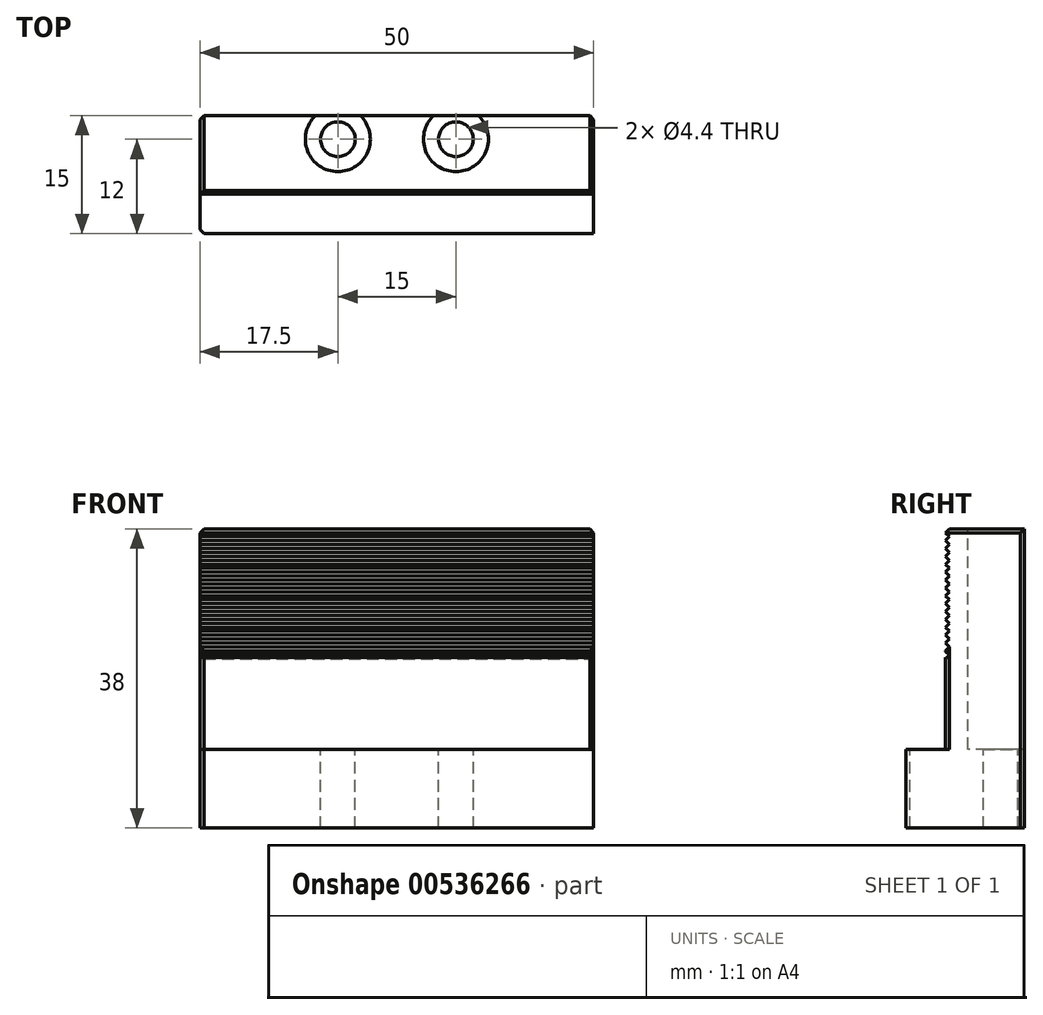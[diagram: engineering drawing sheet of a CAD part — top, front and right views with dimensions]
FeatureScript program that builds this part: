
annotation { "Feature Type Name" : "Feature", "Feature Type Description" : "" }
export const myFeature = defineFeature(function(context is Context, id is Id, definition is map)
    precondition{}
    {
        {
            var Q0;
            Q0=qCreatedBy(makeId("Front.planeOp"),FACE);
            var sketch = newSketch(context, id + "F0", { "sketchPlane" : qUnion([Q0])});
            skLineSegment(sketch, "E0.bottom", {"start": v(0, 0) * mm, "end": v(50, 0) * mm});
            skLineSegment(sketch, "E0.top", {"start": v(0, -38) * mm, "end": v(50, -38) * mm});
            skLineSegment(sketch, "E0.left", {"start": v(0, 0) * mm, "end": v(0, -38) * mm});
            skLineSegment(sketch, "E0.right", {"start": v(50, 0) * mm, "end": v(50, -38) * mm});
            skSolve(sketch);
        }
        {
            var Q0;
            Q0 = qSketchRegion(id + "FYO4Oi6wWd3sull_0", true);
            var Q1;
            Q1=makeQuery(id+"F0.imprint","IMPRINT",FACE,{"disambiguationData":[TD([[makeQuery(id+"F0.imprint","IMPRINT",EDGE,{"derivedFrom":sQuery(id+"F0.wireOp",EDGE,"E0.bottom")}),-1.0]])]});
            extrude(context, id + "F1", {"entities" : qUnion([Q0, Q1]), "depth" : 10 * mm, "offsetDistance" : 25 * mm});
        }
        {
            var Q0;
            Q0=makeQuery(id+"F1.opExtrude","CAP_FACE",FACE,{"disambiguationData":[OSD([sQuery(id+"F0.wireOp",EDGE,"E0.bottom"),sQuery(id+"F0.wireOp",EDGE,"E0.top"),sQuery(id+"F0.wireOp",EDGE,"E0.left"),sQuery(id+"F0.wireOp",EDGE,"E0.right")])],"isStart":false});
            var sketch = newSketch(context, id + "F2", { "sketchPlane" : qUnion([Q0])});
            skLineSegment(sketch, "E1.bottom", {"start": v(0, -38) * mm, "end": v(50, -38) * mm});
            skLineSegment(sketch, "E1.top", {"start": v(0, -28) * mm, "end": v(50, -28) * mm});
            skLineSegment(sketch, "E1.left", {"start": v(0, -38) * mm, "end": v(0, -28) * mm});
            skLineSegment(sketch, "E1.right", {"start": v(50, -38) * mm, "end": v(50, -28) * mm});
            skSolve(sketch);
        }
        {
            var Q0;
            Q0=makeQuery(id+"F2.imprint","IMPRINT",FACE,{"disambiguationData":[TD([[makeQuery(id+"F2.imprint","IMPRINT",EDGE,{"derivedFrom":sQuery(id+"F2.wireOp",EDGE,"E1.bottom")}),1.0]])]});
            extrude(context, id + "F3", {"entities" : qUnion([Q0]), "operationType" : NewBodyOperationType.ADD, "depth" : 5 * mm, "offsetDistance" : 25 * mm});
        }
        {
            var Q0;
            Q0=qCreatedBy(makeId("Top.planeOp"),FACE);
            var sketch = newSketch(context, id + "F4", { "sketchPlane" : qUnion([Q0])});
            skPoint(sketch, "E2", {"position": v(17.5, -3) * mm});
            skPoint(sketch, "E3", {"position": v(32.5, -3) * mm});
            skSolve(sketch);
        }
        {
            var Q0;
            Q0=sQuery(id+"F4.wireOp",VERTEX,"E2");
            var Q1;
            Q1=sQuery(id+"F4.wireOp",VERTEX,"E3");
            var Q2;
            Q2=makeQuery(id+"F1.opExtrude","SWEPT_BODY",BODY,{"disambiguationData":[OSD([sQuery(id+"F0.wireOp",EDGE,"E0.bottom"),sQuery(id+"F0.wireOp",EDGE,"E0.top"),sQuery(id+"F0.wireOp",EDGE,"E0.left"),sQuery(id+"F0.wireOp",EDGE,"E0.right")])]});
            hole(context, id + "F5", {"style" : HoleStyle.C_BORE, "endStyle" : HoleEndStyle.THROUGH, "holeDiameter" : 4.4 * mm, "cBoreDiameter" : 8.25 * mm, "cBoreDepth" : 28 * mm, "isTappedThrough" : true, "tappedDepth" : 50 * mm, "tapClearance" : 3, "startFromSketch" : true, "locations" : qUnion([Q0, Q1]), "scope" : qUnion([Q2])});
        }
        {
            var Q0;
            Q0=makeQuery(id+"F3.boolean.opBoolean","MERGE",FACE,{"derivedFrom":[makeQuery(id+"F1.opExtrude","SWEPT_FACE",FACE,{"disambiguationData":[OSD([sQuery(id+"F0.wireOp",EDGE,"E0.right")])]}),makeQuery(id+"F3.opExtrude","SWEPT_FACE",FACE,{"disambiguationData":[OSD([sQuery(id+"F2.wireOp",EDGE,"E1.right")])]})]});
            var sketch = newSketch(context, id + "F6", { "sketchPlane" : qUnion([Q0])});
            skSolve(sketch);
        }
        {
            var Q0;
            Q0=makeQuery(id+"F1.opExtrude","CAP_EDGE",EDGE,{"disambiguationData":[OSD([sQuery(id+"F0.wireOp",EDGE,"E0.bottom")])],"isStart":false});
            chamfer(context, id + "F7", {"entities" : qUnion([Q0]), "width" : .5 * mm, "tangentPropagation" : true});
        }
        {
            var Q0;
            {var subQ1=sQuery(id+"F0.wireOp",EDGE,"E0.right");Q0=makeQuery(id+"F6.imprint","IMPRINT",FACE,{"disambiguationData":[TD([[makeQuery(id+"F6.imprint","IMPRINT",EDGE,{"derivedFrom":makeQuery(id+"F1.opExtrude","CAP_EDGE",EDGE,{"disambiguationData":[OSD([subQ1])],"isStart":true})}),-1.0]])]});}
            var sketch = newSketch(context, id + "F8", { "sketchPlane" : qUnion([Q0])});
            skPoint(sketch, "E4", {"position": v(-10.03, -0.5) * mm});
            skPoint(sketch, "E5", {"position": v(-10, -1.5) * mm});
            skPoint(sketch, "E6", {"position": v(-9.5, -1) * mm});
            skLineSegment(sketch, "E7", {"start": v(-10.03, -0.5) * mm, "end": v(-9.5, -1) * mm});
            skLineSegment(sketch, "E8", {"start": v(-10, -1.5) * mm, "end": v(-10.03, -0.5) * mm});
            skLineSegment(sketch, "E9", {"start": v(-9.5, -1) * mm, "end": v(-10, -1.5) * mm});
            skSolve(sketch);
        }
        {
            var Q0;
            Q0 = qSketchRegion(id + "FoSwPSxo0hVtyaT_1", true);
            var Q1;
            {var subQ0=sQuery(id+"F8.wireOp",EDGE,"E9");Q1=makeQuery(id+"F8.imprint","IMPRINT",FACE,{"disambiguationData":[TD([[makeQuery(id+"F8.imprint","IMPRINT",EDGE,{"derivedFrom":subQ0}),-1.0]])]});}
            extrude(context, id + "F9", {"entities" : qUnion([Q0, Q1]), "operationType" : NewBodyOperationType.REMOVE, "endBound" : BoundingType.THROUGH_ALL, "oppositeDirection" : true, "depth" : 50 * mm, "offsetDistance" : 25 * mm});
        }
        {
            var Q0;
            Q0=makeQuery(id+"F3.boolean.opBoolean","MERGE",FACE,{"derivedFrom":[makeQuery(id+"F1.opExtrude","SWEPT_FACE",FACE,{"disambiguationData":[OSD([sQuery(id+"F0.wireOp",EDGE,"E0.left")])]}),makeQuery(id+"F3.opExtrude","SWEPT_FACE",FACE,{"disambiguationData":[OSD([sQuery(id+"F2.wireOp",EDGE,"E1.left")])]})]});
            var sketch = newSketch(context, id + "F10", { "sketchPlane" : qUnion([Q0])});
            skPoint(sketch, "E10", {"position": v(10, -2.5) * mm});
            skPoint(sketch, "E11", {"position": v(9.5, -2) * mm});
            skLineSegment(sketch, "E12", {"start": v(10, -1.5) * mm, "end": v(9.5, -2) * mm});
            skLineSegment(sketch, "E13", {"start": v(9.5, -2) * mm, "end": v(10, -2.5) * mm});
            skLineSegment(sketch, "E14", {"start": v(10, -2.5) * mm, "end": v(10, -1.5) * mm});
            skSolve(sketch);
        }
        {
            var Q0;
            Q0=makeQuery(id+"F10.imprint","IMPRINT",FACE,{"disambiguationData":[TD([[makeQuery(id+"F10.imprint","IMPRINT",EDGE,{"derivedFrom":sQuery(id+"F10.wireOp",EDGE,"E12")}),1.0]])]});
            extrude(context, id + "F11", {"entities" : qUnion([Q0]), "operationType" : NewBodyOperationType.REMOVE, "endBound" : BoundingType.THROUGH_ALL, "oppositeDirection" : true, "depth" : 25 * mm, "offsetDistance" : 25 * mm});
        }
        {
            var Q0;
            Q0=makeQuery(id+"F3.boolean.opBoolean","MERGE",FACE,{"derivedFrom":[makeQuery(id+"F1.opExtrude","SWEPT_FACE",FACE,{"disambiguationData":[OSD([sQuery(id+"F0.wireOp",EDGE,"E0.left")])]}),makeQuery(id+"F3.opExtrude","SWEPT_FACE",FACE,{"disambiguationData":[OSD([sQuery(id+"F2.wireOp",EDGE,"E1.left")])]})]});
            var sketch = newSketch(context, id + "F12", { "sketchPlane" : qUnion([Q0])});
            skPoint(sketch, "E15", {"position": v(9.5, -3) * mm});
            skPoint(sketch, "E16", {"position": v(10, -2.5) * mm});
            skPoint(sketch, "E17", {"position": v(10, -3.5) * mm});
            skLineSegment(sketch, "E18", {"start": v(10, -2.5) * mm, "end": v(9.5, -3) * mm});
            skLineSegment(sketch, "E19", {"start": v(9.5, -3) * mm, "end": v(10, -3.5) * mm});
            skLineSegment(sketch, "E20", {"start": v(10, -3.5) * mm, "end": v(10, -2.5) * mm});
            skSolve(sketch);
        }
        {
            var Q0;
            Q0 = qSketchRegion(id + "F12", true);
            var Q1;
            Q1=makeQuery(id+"F12.imprint","IMPRINT",FACE,{"disambiguationData":[TD([[makeQuery(id+"F12.imprint","IMPRINT",EDGE,{"derivedFrom":sQuery(id+"F12.wireOp",EDGE,"E18")}),1.0]])]});
            extrude(context, id + "F13", {"entities" : qUnion([Q0, Q1]), "operationType" : NewBodyOperationType.REMOVE, "endBound" : BoundingType.THROUGH_ALL, "oppositeDirection" : true, "depth" : 25 * mm, "offsetDistance" : 25 * mm});
        }
        {
            var Q0;
            Q0=makeQuery(id+"F3.boolean.opBoolean","MERGE",FACE,{"derivedFrom":[makeQuery(id+"F1.opExtrude","SWEPT_FACE",FACE,{"disambiguationData":[OSD([sQuery(id+"F0.wireOp",EDGE,"E0.left")])]}),makeQuery(id+"F3.opExtrude","SWEPT_FACE",FACE,{"disambiguationData":[OSD([sQuery(id+"F2.wireOp",EDGE,"E1.left")])]})]});
            var sketch = newSketch(context, id + "F14", { "sketchPlane" : qUnion([Q0])});
            skPoint(sketch, "E21", {"position": v(10, -4.5) * mm});
            skPoint(sketch, "E22", {"position": v(9.5, -4) * mm});
            skPoint(sketch, "E23", {"position": v(10, -3.5) * mm});
            skLineSegment(sketch, "E24", {"start": v(10, -3.5) * mm, "end": v(9.5, -4) * mm});
            skLineSegment(sketch, "E25", {"start": v(9.5, -4) * mm, "end": v(10, -4.5) * mm});
            skLineSegment(sketch, "E26", {"start": v(10, -3.5) * mm, "end": v(10, -4.5) * mm});
            skSolve(sketch);
        }
        {
            var Q0;
            Q0 = qSketchRegion(id + "F14", true);
            var Q1;
            Q1=makeQuery(id+"F14.imprint","IMPRINT",FACE,{"disambiguationData":[TD([[makeQuery(id+"F14.imprint","IMPRINT",EDGE,{"derivedFrom":sQuery(id+"F14.wireOp",EDGE,"E24")}),1.0]])]});
            extrude(context, id + "F15", {"entities" : qUnion([Q0, Q1]), "operationType" : NewBodyOperationType.REMOVE, "endBound" : BoundingType.THROUGH_ALL, "oppositeDirection" : true, "depth" : 25 * mm, "offsetDistance" : 25 * mm});
        }
        {
            var Q0;
            Q0=makeQuery(id+"F3.boolean.opBoolean","MERGE",FACE,{"derivedFrom":[makeQuery(id+"F1.opExtrude","SWEPT_FACE",FACE,{"disambiguationData":[OSD([sQuery(id+"F0.wireOp",EDGE,"E0.left")])]}),makeQuery(id+"F3.opExtrude","SWEPT_FACE",FACE,{"disambiguationData":[OSD([sQuery(id+"F2.wireOp",EDGE,"E1.left")])]})]});
            var sketch = newSketch(context, id + "F16", { "sketchPlane" : qUnion([Q0])});
            skPoint(sketch, "E27", {"position": v(10, -5.5) * mm});
            skPoint(sketch, "E28", {"position": v(9.5, -5) * mm});
            skLineSegment(sketch, "E29", {"start": v(9.5, -5) * mm, "end": v(10, -4.5) * mm});
            skLineSegment(sketch, "E30", {"start": v(10, -5.5) * mm, "end": v(10, -4.5) * mm});
            skLineSegment(sketch, "E31", {"start": v(9.5, -5) * mm, "end": v(10, -5.5) * mm});
            skSolve(sketch);
        }
        {
            var Q0;
            Q0 = qSketchRegion(id + "F16", true);
            extrude(context, id + "F17", {"entities" : qUnion([Q0]), "depth" : 25 * mm, "offsetDistance" : 25 * mm});
        }
        {
            var Q0;
            Q0 = qSketchRegion(id + "F8XrWfeoZaRGUGP_1", true);
            var Q1;
            Q1=makeQuery(id+"F17.opExtrude","CAP_FACE",FACE,{"disambiguationData":[OSD([sQuery(id+"F16.wireOp",EDGE,"E29"),sQuery(id+"F16.wireOp",EDGE,"E30"),sQuery(id+"F16.wireOp",EDGE,"E31")])],"isStart":false});
            extrude(context, id + "F18", {"entities" : qUnion([Q0, Q1]), "operationType" : NewBodyOperationType.REMOVE, "endBound" : BoundingType.THROUGH_ALL, "oppositeDirection" : true, "depth" : 25 * mm, "offsetDistance" : 25 * mm});
        }
        {
            var Q0;
            {var subQ2=sQuery(id+"F8.wireOp",EDGE,"E9");Q0=makeQuery(id+"F8.imprint","IMPRINT",FACE,{"disambiguationData":[TD([[makeQuery(id+"F8.imprint","IMPRINT",EDGE,{"derivedFrom":subQ2}),1.0]])]});}
            var sketch = newSketch(context, id + "F19", { "sketchPlane" : qUnion([Q0])});
            skPoint(sketch, "E32", {"position": v(-10, -5.5) * mm});
            skPoint(sketch, "E33", {"position": v(-9.5, -4) * mm});
            skPoint(sketch, "E34", {"position": v(-9.5, -5) * mm});
            skLineSegment(sketch, "E35", {"start": v(-9.5, -5) * mm, "end": v(-10, -5.5) * mm});
            skLineSegment(sketch, "E36", {"start": v(-10, -5.5) * mm, "end": v(-10, -4.53) * mm});
            skLineSegment(sketch, "E37", {"start": v(-10, -4.53) * mm, "end": v(-9.5, -5) * mm});
            skSolve(sketch);
        }
        {
            var Q0;
            Q0 = qSketchRegion(id + "F19", true);
            extrude(context, id + "F20", {"entities" : qUnion([Q0]), "operationType" : NewBodyOperationType.REMOVE, "endBound" : BoundingType.THROUGH_ALL, "oppositeDirection" : true, "depth" : 25 * mm, "offsetDistance" : 25 * mm});
        }
        {
            var Q0;
            Q0=makeQuery(id+"F3.boolean.opBoolean","MERGE",FACE,{"derivedFrom":[makeQuery(id+"F1.opExtrude","SWEPT_FACE",FACE,{"disambiguationData":[OSD([sQuery(id+"F0.wireOp",EDGE,"E0.left")])]}),makeQuery(id+"F3.opExtrude","SWEPT_FACE",FACE,{"disambiguationData":[OSD([sQuery(id+"F2.wireOp",EDGE,"E1.left")])]})]});
            var sketch = newSketch(context, id + "F21", { "sketchPlane" : qUnion([Q0])});
            skPoint(sketch, "E38", {"position": v(10, -6.5) * mm});
            skPoint(sketch, "E39", {"position": v(9.5, -6) * mm});
            skPoint(sketch, "E40", {"position": v(10, -5.5) * mm});
            skPoint(sketch, "E41", {"position": v(10, -7.5) * mm});
            skPoint(sketch, "E42", {"position": v(10, -8.5) * mm});
            skPoint(sketch, "E43", {"position": v(10, -9.5) * mm});
            skPoint(sketch, "E44", {"position": v(10, -10.5) * mm});
            skPoint(sketch, "E45", {"position": v(10, -11.5) * mm});
            skPoint(sketch, "E46", {"position": v(10, -12.5) * mm});
            skPoint(sketch, "E47", {"position": v(10, -13.5) * mm});
            skPoint(sketch, "E48", {"position": v(10, -14.5) * mm});
            skPoint(sketch, "E49", {"position": v(10, -15.5) * mm});
            skPoint(sketch, "E50", {"position": v(9.5, -7) * mm});
            skPoint(sketch, "E51", {"position": v(9.5, -8) * mm});
            skPoint(sketch, "E52", {"position": v(9.5, -9) * mm});
            skPoint(sketch, "E53", {"position": v(9.5, -10) * mm});
            skPoint(sketch, "E54", {"position": v(9.5, -11) * mm});
            skPoint(sketch, "E55", {"position": v(9.5, -12) * mm});
            skPoint(sketch, "E56", {"position": v(9.5, -13) * mm});
            skPoint(sketch, "E57", {"position": v(9.5, -14) * mm});
            skPoint(sketch, "E58", {"position": v(9.5, -15) * mm});
            skLineSegment(sketch, "E59", {"start": v(10, -5.5) * mm, "end": v(10, -15.5) * mm});
            skLineSegment(sketch, "E60", {"start": v(10, -5.5) * mm, "end": v(9.5, -6) * mm});
            skLineSegment(sketch, "E61", {"start": v(9.5, -6) * mm, "end": v(10, -6.5) * mm});
            skLineSegment(sketch, "E62", {"start": v(9.5, -7) * mm, "end": v(10, -6.5) * mm});
            skLineSegment(sketch, "E63", {"start": v(9.5, -7) * mm, "end": v(10, -7.5) * mm});
            skLineSegment(sketch, "E64", {"start": v(10, -7.5) * mm, "end": v(9.5, -8) * mm});
            skLineSegment(sketch, "E65", {"start": v(9.5, -8) * mm, "end": v(10, -8.5) * mm});
            skLineSegment(sketch, "E66", {"start": v(10, -8.5) * mm, "end": v(9.5, -9) * mm});
            skLineSegment(sketch, "E67", {"start": v(9.5, -9) * mm, "end": v(10, -9.5) * mm});
            skLineSegment(sketch, "E68", {"start": v(10, -9.5) * mm, "end": v(9.5, -10) * mm});
            skLineSegment(sketch, "E69", {"start": v(9.5, -10) * mm, "end": v(10, -10.5) * mm});
            skLineSegment(sketch, "E70", {"start": v(10, -10.5) * mm, "end": v(9.5, -11) * mm});
            skLineSegment(sketch, "E71", {"start": v(9.5, -11) * mm, "end": v(10, -11.5) * mm});
            skLineSegment(sketch, "E72", {"start": v(10, -11.5) * mm, "end": v(9.5, -12) * mm});
            skLineSegment(sketch, "E73", {"start": v(9.5, -12) * mm, "end": v(10, -12.5) * mm});
            skLineSegment(sketch, "E74", {"start": v(10, -12.5) * mm, "end": v(9.5, -13) * mm});
            skLineSegment(sketch, "E75", {"start": v(9.5, -13) * mm, "end": v(10, -13.5) * mm});
            skLineSegment(sketch, "E76", {"start": v(10, -13.5) * mm, "end": v(9.5, -14) * mm});
            skLineSegment(sketch, "E77", {"start": v(9.5, -14) * mm, "end": v(10, -14.5) * mm});
            skLineSegment(sketch, "E78", {"start": v(9.5, -15) * mm, "end": v(10, -14.5) * mm});
            skLineSegment(sketch, "E79", {"start": v(9.5, -15) * mm, "end": v(10, -15.5) * mm});
            skSolve(sketch);
        }
        {
            var Q0;
            Q0 = qSketchRegion(id + "F21", true);
            extrude(context, id + "F22", {"entities" : qUnion([Q0]), "operationType" : NewBodyOperationType.REMOVE, "endBound" : BoundingType.THROUGH_ALL, "oppositeDirection" : true, "depth" : 25 * mm, "offsetDistance" : 25 * mm});
        }
        {
            var Q0;
            Q0=makeQuery(id+"F1.opExtrude","SWEPT_EDGE",EDGE,{"disambiguationData":[OSD([sQuery(id+"F0.wireOp",EDGE,"E0.bottom"),sQuery(id+"F0.wireOp",EDGE,"E0.left")])]});
            var Q1;
            {var subQ0=makeQuery(id+"F3.opExtrude","SWEPT_FACE",FACE,{"disambiguationData":[OSD([sQuery(id+"F2.wireOp",EDGE,"E1.top")])]});var subQ1=sQuery(id+"F0.wireOp",EDGE,"E0.left");Q1=makeQuery(id+"F20.boolean.opBoolean","SPLIT",EDGE,{"disambiguationData":[TD([subQ0])],"derivedFrom":makeQuery(id+"F9.boolean.opBoolean","SPLIT",EDGE,{"disambiguationData":[TD([subQ0])],"derivedFrom":makeQuery(id+"F1.opExtrude","CAP_EDGE",EDGE,{"disambiguationData":[OSD([subQ1])],"isStart":false})})});}
            var Q2;
            Q2=makeQuery(id+"F3.opExtrude","CAP_EDGE",EDGE,{"disambiguationData":[OSD([sQuery(id+"F2.wireOp",EDGE,"E1.left")])],"isStart":false});
            var Q3;
            Q3=makeQuery(id+"F1.opExtrude","CAP_EDGE",EDGE,{"disambiguationData":[OSD([sQuery(id+"F0.wireOp",EDGE,"E0.left")])],"isStart":true});
            var Q4;
            {var subQ1=makeQuery(id+"F3.opExtrude","SWEPT_FACE",FACE,{"disambiguationData":[OSD([sQuery(id+"F2.wireOp",EDGE,"E1.top")])]});var subQ2=sQuery(id+"F0.wireOp",EDGE,"E0.right");Q4=makeQuery(id+"F20.boolean.opBoolean","SPLIT",EDGE,{"disambiguationData":[TD([subQ1])],"derivedFrom":makeQuery(id+"F9.boolean.opBoolean","SPLIT",EDGE,{"disambiguationData":[TD([subQ1])],"derivedFrom":makeQuery(id+"F1.opExtrude","CAP_EDGE",EDGE,{"disambiguationData":[OSD([subQ2])],"isStart":false})})});}
            var Q5;
            Q5=makeQuery(id+"F1.opExtrude","CAP_EDGE",EDGE,{"disambiguationData":[OSD([sQuery(id+"F0.wireOp",EDGE,"E0.right")])],"isStart":true});
            var Q6;
            Q6=makeQuery(id+"F1.opExtrude","SWEPT_EDGE",EDGE,{"disambiguationData":[OSD([sQuery(id+"F0.wireOp",EDGE,"E0.bottom"),sQuery(id+"F0.wireOp",EDGE,"E0.right")])]});
            chamfer(context, id + "F23", {"entities" : qUnion([Q0, Q1, Q2, Q3, Q4, Q5, Q6]), "width" : .5 * mm, "tangentPropagation" : true});
        }
        {
            var Q0;
            {var subQ1=sQuery(id+"F0.wireOp",EDGE,"E0.right");Q0=makeQuery(id+"F6.imprint","IMPRINT",FACE,{"disambiguationData":[TD([[makeQuery(id+"F6.imprint","IMPRINT",EDGE,{"derivedFrom":makeQuery(id+"F1.opExtrude","CAP_EDGE",EDGE,{"disambiguationData":[OSD([subQ1])],"isStart":true})}),-1.0]])]});}
            var sketch = newSketch(context, id + "F24", { "sketchPlane" : qUnion([Q0])});
            skPoint(sketch, "E80", {"position": v(-10, -16.5) * mm});
            skPoint(sketch, "E81", {"position": v(-9.49, -16) * mm});
            skLineSegment(sketch, "E82", {"start": v(-9.49, -16) * mm, "end": v(-10.06, -15.53) * mm});
            skLineSegment(sketch, "E83", {"start": v(-10.06, -15.53) * mm, "end": v(-10, -16.5) * mm});
            skLineSegment(sketch, "E84", {"start": v(-10, -16.5) * mm, "end": v(-9.49, -16) * mm});
            skSolve(sketch);
        }
        {
            var Q0;
            {var subQ0=sQuery(id+"F24.wireOp",EDGE,"E84");Q0=makeQuery(id+"F24.imprint","IMPRINT",FACE,{"disambiguationData":[TD([[makeQuery(id+"F24.imprint","IMPRINT",EDGE,{"derivedFrom":subQ0}),1.0]])]});}
            extrude(context, id + "F25", {"entities" : qUnion([Q0]), "operationType" : NewBodyOperationType.REMOVE, "endBound" : BoundingType.THROUGH_ALL, "oppositeDirection" : true, "depth" : 25 * mm, "offsetDistance" : 25 * mm});
        }
    });
